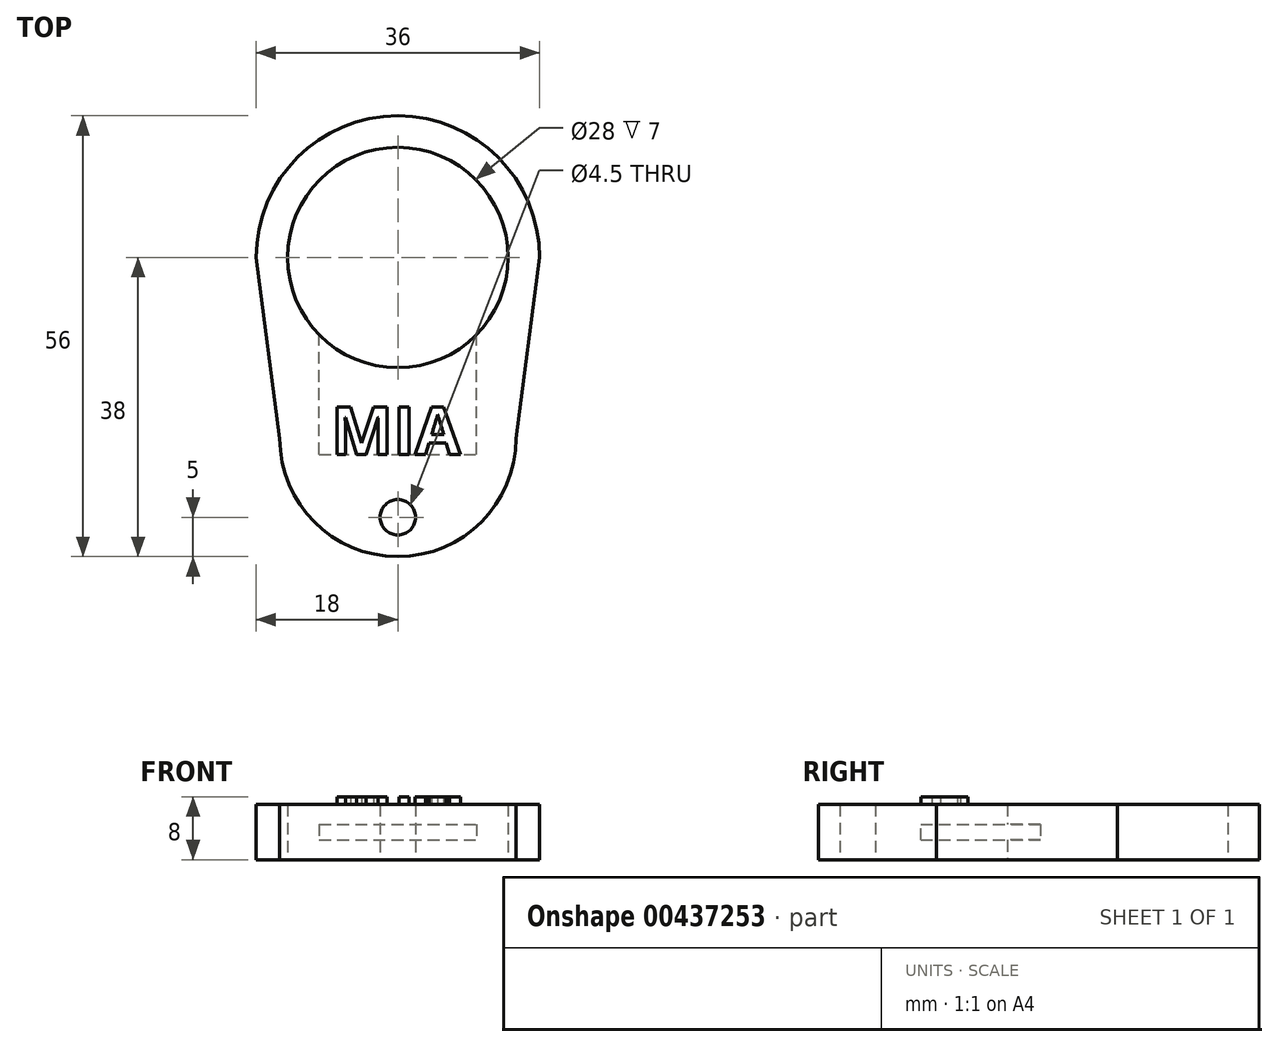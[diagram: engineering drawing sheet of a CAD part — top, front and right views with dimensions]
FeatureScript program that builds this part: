
annotation { "Feature Type Name" : "Feature", "Feature Type Description" : "" }
export const myFeature = defineFeature(function(context is Context, id is Id, definition is map)
    precondition{}
    {
        {
            var Q0;
            Q0=qCreatedBy(makeId("Top.planeOp"),FACE);
            var sketch = newSketch(context, id + "F0", { "sketchPlane" : qUnion([Q0])});
            skLineSegment(sketch, "E0", {"start": v(0, 44.1) * mm, "end": v(0, -68.44) * mm, "construction": true});
            skCircle(sketch, "E1", {"center": v(0, 0) * mm, "radius": 14 * mm});
            skLineSegment(sketch, "E2", {"start": v(-47.03, -23) * mm, "end": v(50.85, -23) * mm, "construction": true});
            skPoint(sketch, "E3", {"position": v(-15, -23) * mm});
            skPoint(sketch, "E4", {"position": v(15, -23) * mm});
            skPoint(sketch, "E5", {"position": v(-18, 0) * mm});
            skPoint(sketch, "E6", {"position": v(18, 0) * mm});
            skLineSegment(sketch, "E7", {"start": v(-18, 0) * mm, "end": v(-15, -23) * mm});
            skLineSegment(sketch, "E8", {"start": v(18, 0) * mm, "end": v(15, -23) * mm});
            skArc(sketch, "E9.trimOffspring", {"start": v(-15, -23) * mm, "mid": v(0, -38) * mm, "end": v(15, -23) * mm});
            skArc(sketch, "E10.trimOffspring", {"start": v(18, 0) * mm, "mid": v(0, 18) * mm, "end": v(-18, 0) * mm});
            skSolve(sketch);
        }
        {
            var Q0;
            Q0 = qSketchRegion(id + "F0", true);
            extrude(context, id + "F1", {"entities" : qUnion([Q0]), "depth" : 7 * mm});
        }
        {
            var Q0;
            Q0=qCreatedBy(makeId("Front.planeOp"),FACE);
            var sketch = newSketch(context, id + "F2", { "sketchPlane" : qUnion([Q0])});
            skLineSegment(sketch, "E11", {"start": v(0, 0) * mm, "end": v(0, 18.27) * mm, "construction": true});
            skLineSegment(sketch, "E12.bottom", {"start": v(-10, 2.5) * mm, "end": v(10, 2.5) * mm});
            skLineSegment(sketch, "E12.top", {"start": v(-10, 4.5) * mm, "end": v(10, 4.5) * mm});
            skLineSegment(sketch, "E12.left", {"start": v(-10, 2.5) * mm, "end": v(-10, 4.5) * mm});
            skLineSegment(sketch, "E12.right", {"start": v(10, 2.5) * mm, "end": v(10, 4.5) * mm});
            skPoint(sketch, "E12.middle", {"position": v(0, 3.5) * mm});
            skSolve(sketch);
        }
        {
            var Q0;
            Q0 = qSketchRegion(id + "F2", true);
            extrude(context, id + "F3", {"entities" : qUnion([Q0]), "operationType" : NewBodyOperationType.REMOVE, "depth" : 25 * mm});
        }
        {
            var Q0;
            Q0=makeQuery(id+"F1.opExtrude","CAP_FACE",FACE,{"disambiguationData":[OSD([sQuery(id+"F0.wireOp",EDGE,"E1"),sQuery(id+"F0.wireOp",EDGE,"E7"),sQuery(id+"F0.wireOp",EDGE,"E8"),sQuery(id+"F0.wireOp",EDGE,"E9.trimOffspring"),sQuery(id+"F0.wireOp",EDGE,"E10.trimOffspring")])],"isStart":true});
            var sketch = newSketch(context, id + "F4", { "sketchPlane" : qUnion([Q0])});
            skLineSegment(sketch, "E13", {"start": v(0, 0) * mm, "end": v(0, 51.24) * mm, "construction": true});
            skCircle(sketch, "E14", {"center": v(0, 33) * mm, "radius": 2.25 * mm});
            skSolve(sketch);
        }
        {
            var Q0;
            Q0 = qSketchRegion(id + "F4", true);
            extrude(context, id + "F5", {"entities" : qUnion([Q0]), "operationType" : NewBodyOperationType.REMOVE, "oppositeDirection" : true, "depth" : 25 * mm});
        }
        {
            var Q0;
            Q0=makeQuery(id+"F1.opExtrude","CAP_FACE",FACE,{"disambiguationData":[OSD([sQuery(id+"F0.wireOp",EDGE,"E1"),sQuery(id+"F0.wireOp",EDGE,"E7"),sQuery(id+"F0.wireOp",EDGE,"E8"),sQuery(id+"F0.wireOp",EDGE,"E9.trimOffspring"),sQuery(id+"F0.wireOp",EDGE,"E10.trimOffspring")])],"isStart":false});
            var sketch = newSketch(context, id + "F6", { "sketchPlane" : qUnion([Q0])});
            skText(sketch, "E15", { "text": "MIA", "fontName": "OpenSans-Bold.ttf"});
            const initialGuessF6  = {"E15": [-0.0085, -0.025, 1, 0, 0.00603]};
            skSetInitialGuess(sketch, initialGuessF6);
            skSolve(sketch);
        }
        {
            var Q0;
            Q0 = qSketchRegion(id + "F6", true);
            extrude(context, id + "F7", {"entities" : qUnion([Q0]), "operationType" : NewBodyOperationType.ADD, "depth" : 1 * mm});
        }
    });
